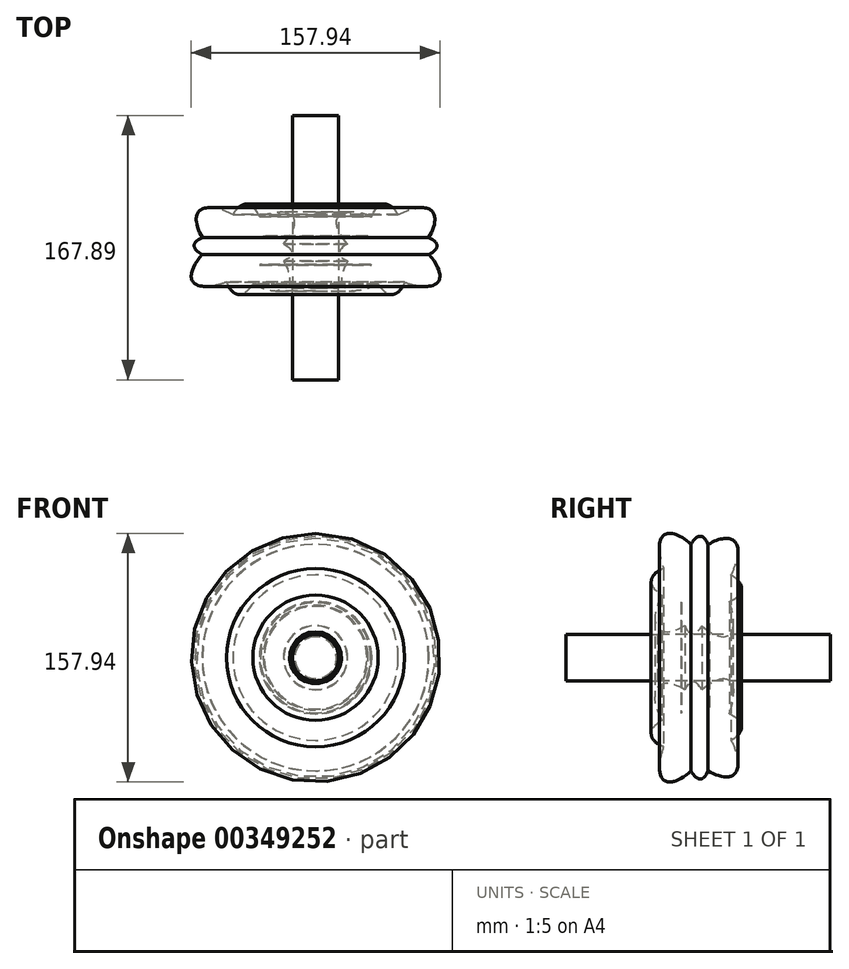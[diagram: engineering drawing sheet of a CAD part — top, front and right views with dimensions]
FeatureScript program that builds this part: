
annotation { "Feature Type Name" : "Feature", "Feature Type Description" : "" }
export const myFeature = defineFeature(function(context is Context, id is Id, definition is map)
    precondition{}
    {
        {
            var Q0;
            Q0=qCreatedBy(makeId("Top.planeOp"),FACE);
            var sketch = newSketch(context, id + "F0", { "sketchPlane" : qUnion([Q0])});
            skEllipticalArc(sketch, "E0", {});
            skEllipticalArc(sketch, "E1", {});
            skEllipticalArc(sketch, "E2", {});
            skEllipticalArc(sketch, "E3.trimOffspring", {});
            skEllipticalArc(sketch, "E4.trimOffspring", {});
            skEllipticalArc(sketch, "E5.trimOffspring", {});
            skEllipticalArc(sketch, "E6.trimOffspring", {});
            skEllipticalArc(sketch, "E7.trimOffspring", {});
            skEllipticalArc(sketch, "E8.trimOffspring", {});
            skEllipticalArc(sketch, "E9.trimOffspring", {});
            skEllipticalArc(sketch, "E10.trimOffspring", {});
            skEllipticalArc(sketch, "E11.trimOffspring", {});
            skEllipticalArc(sketch, "E12.trimOffspring", {});
            skEllipticalArc(sketch, "E13.trimOffspring", {});
            skEllipticalArc(sketch, "E14.trimOffspring", {});
            skEllipticalArc(sketch, "E15.trimOffspring", {});
            skLineSegment(sketch, "E16", {"start": v(0, 50.65) * mm, "end": v(0, 0) * mm});
            const initialGuessF0  = {"E0": [-0.04613479971885681, 0.024519193917512894, 0.8436614776025686, 0.5368755081110059, 0.03785816654708674, 0.01417188208934379, 2.246258807500407, 4.155884634578479], "E1": [-0.04613479971885681, 0.024519193917512894, -0.7617232832571665, 0.6479024924662062, 0.03684805923891022, 0.0147704866237621, 2.1156394124687434, 3.990073310051104], "E2": [-0.04613479971885681, 0.024519193917512894, 0.996545761551508, -0.08304544017419067, 0.031078970682046018, 0.009681649898081882, 2.5770953689085445, 3.7479627287171504], "E3.trimOffspring": [-0.04613479971885681, 0.024519193917512894, 0.10061045905630307, 0.9949258944908812, 0.028859704482056603, 0.012622317414327773, 1.892535852355951, 1.910179911513776], "E4.trimOffspring": [-0.04613479971885681, 0.024519193917512894, 0.996545761551508, -0.08304544017419067, 0.031078970682046018, 0.009681649898081882, 5.090398154390552, 5.1044162052877], "E5.trimOffspring": [-0.04613479971885681, 0.024519193917512894, 0.996545761551508, -0.08304544017419067, 0.031078970682046018, 0.009681649898081882, 4.288423579471778, 4.311305341638427], "E6.trimOffspring": [-0.04613479971885681, 0.024519193917512894, 0.10061045905630307, 0.9949258944908812, 0.028859704482056603, 0.012622317414327773, 2.428602028849709, 3.8850967671631484], "E7.trimOffspring": [-0.04613479971885681, 0.024519193917512894, 0.8436614776025686, 0.5368755081110059, 0.03785816654708674, 0.01417188208934379, 4.809950202966133, 4.8255505090277095], "E8.trimOffspring": [-0.04613479971885681, 0.024519193917512894, 0.10061045905630307, 0.9949258944908812, 0.028859704482056603, 0.012622317414327773, 4.404846697770304, 4.4165951177725775], "E9.trimOffspring": [-0.04613479971885681, 0.024519193917512894, 0.996545761551508, -0.08304544017419067, 0.031078970682046018, 0.009681649898081882, 5.718688022498338, 0.6063700751273579], "E10.trimOffspring": [-0.04613479971885681, 0.024519193917512894, 0.8436614776025686, 0.5368755081110059, 0.03785816654708674, 0.01417188208934379, 5.3878514610902, 1.0142919809886863], "E11.trimOffspring": [-0.04613479971885681, 0.024519193917512894, -0.7617232832571665, 0.6479024924662062, 0.03684805923891022, 0.0147704866237621, 4.569326225740193, 4.594353997514626], "E12.trimOffspring": [-0.04613479971885681, 0.024519193917512894, 0.10061045905630307, 0.9949258944908812, 0.028859704482056603, 0.012622317414327773, 5.034128505945745, 5.051772565103569], "E13.trimOffspring": [-0.04613479971885681, 0.024519193917512894, 0.10061045905630307, 0.9949258944908812, 0.028859704482056603, 0.012622317414327773, 5.570194682439501, 0.7435041135733556], "E14.trimOffspring": [-0.04613479971885681, 0.024519193917512894, -0.7617232832571665, 0.6479024924662062, 0.03684805923891022, 0.0147704866237621, 5.2572320660585365, 0.8484806564613123], "E15.trimOffspring": [-0.04613479971885681, 0.024519193917512894, 0.996545761551508, -0.08304544017419067, 0.031078970682046018, 0.009681649898081882, 1.146830925881983, 1.1697126880486344]};
            skSetInitialGuess(sketch, initialGuessF0);
            skSolve(sketch);
        }
        {
            var Q0;
            Q0 = qSketchRegion(id + "F0", true);
            var Q1;
            Q1=sQuery(id+"F0.wireOp",EDGE,"E16");
            revolve(context, id + "F1", {"entities" : qUnion([Q0]), "axis" : qUnion([Q1]), "revolveType" : RevolveType.FULL});
        }
        {
            var Q0;
            Q0=qCreatedBy(makeId("Front.planeOp"),FACE);
            var sketch = newSketch(context, id + "F2", { "sketchPlane" : qUnion([Q0])});
            skCircle(sketch, "E17", {"center": v(0, 0) * mm, "radius": 14.7 * mm});
            skSolve(sketch);
        }
        {
            var Q0;
            Q0 = qSketchRegion(id + "F2", true);
            extrude(context, id + "F3", {"entities" : qUnion([Q0]), "depth" : 58.42 * mm});
        }
        {
            var Q0;
            Q0 = qSketchRegion(id + "F2", true);
            extrude(context, id + "F4", {"entities" : qUnion([Q0]), "oppositeDirection" : true, "depth" : 109.47 * mm});
        }
    });
